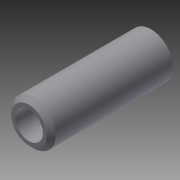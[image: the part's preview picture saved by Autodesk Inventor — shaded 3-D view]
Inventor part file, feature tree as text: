
AUTODESK INVENTOR PART (.ipt)
format: ipt  version: 2015 SP1 (Build 190203100, 203)  size: 93,184 bytes
history: native  units: in
note: dims shown in document units (in); Inventor stores cm internally (conversion verified against a paired STEP export)
features: sketch x3, extrude x2, hole x1, chamfer x1
ambient origin geometry x8: Origin, YZ Plane, XZ Plane, XY Plane, X Axis, Y Axis, Z Axis, Center Point
bodies: Solid1 (feature_tree)
feature tree (7):
  extrude  "Extrusion1"  Depth=2.75in TaperAngle=0.0deg
  extrude  "Extrusion2"  Depth=1.8in TaperAngle=0.0deg
  hole  "Hole1"  [1 undecoded]
  chamfer  "Chamfer1"  [1 undecoded]
  sketch  "Sketch1"  dims[d0=1.0in d1=2.75in d2=0.0in]
  sketch  "Sketch2"  dims[d3=0.625in d4=1.8in d5=0.0in]
  sketch  "Sketch3"  dims[d6=0.417in d7=1.0in d8=0.375in d9=0.25in d10=0.5635in d11=1.385in d12=0.8108in d13=0.1in d14=0.125in d15=45.0deg]
note: 2 required parameter values undecoded (feature->parameter linkage not recoverable at this tier; creation-order binding heuristic only, values carry confidence <= 0.55)
